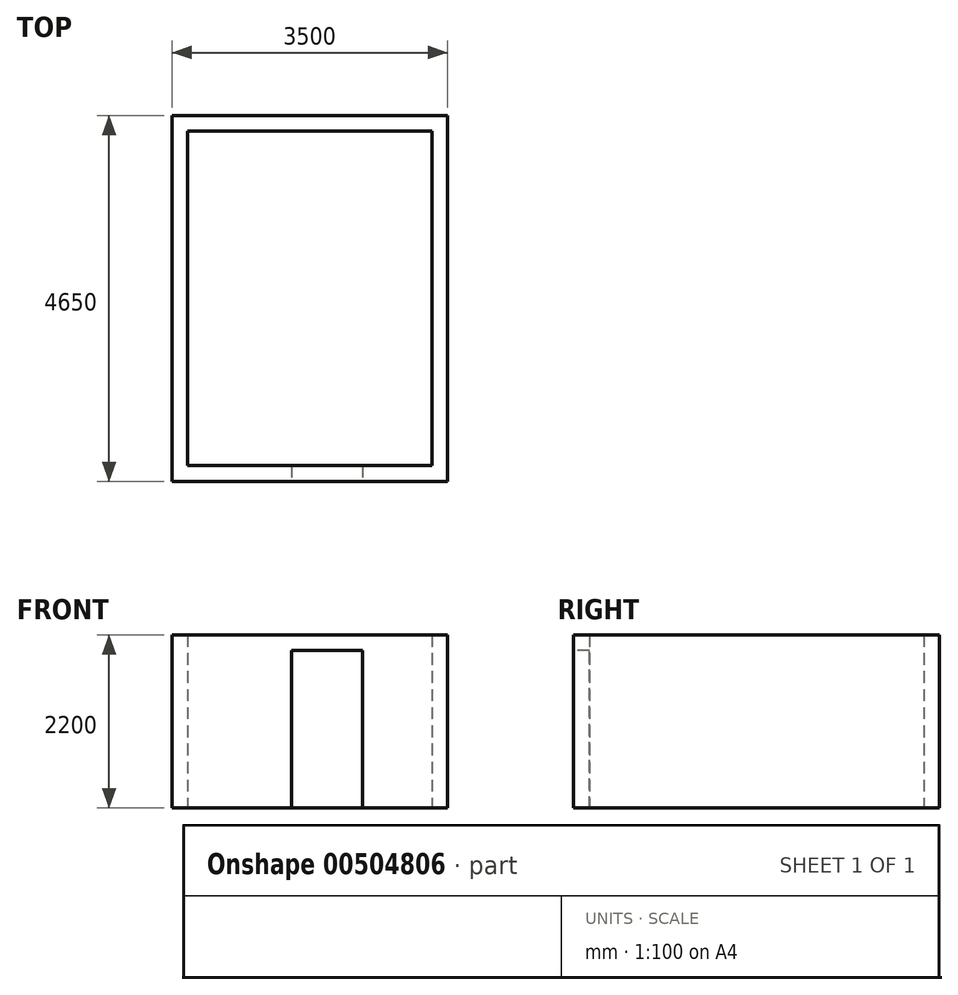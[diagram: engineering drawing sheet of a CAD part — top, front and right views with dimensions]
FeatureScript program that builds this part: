
annotation { "Feature Type Name" : "Feature", "Feature Type Description" : "" }
export const myFeature = defineFeature(function(context is Context, id is Id, definition is map)
    precondition{}
    {
        {
            var Q0;
            Q0=qCreatedBy(makeId("Top.planeOp"),FACE);
            var sketch = newSketch(context, id + "F0", { "sketchPlane" : qUnion([Q0])});
            skLineSegment(sketch, "E0.bottom", {"start": v(500, 4755.13) * mm, "end": v(-3000, 4755.13) * mm});
            skLineSegment(sketch, "E0.top", {"start": v(500, 105.13) * mm, "end": v(-3000, 105.13) * mm});
            skLineSegment(sketch, "E0.right", {"start": v(-3000, 4755.13) * mm, "end": v(-3000, 105.13) * mm});
            skLineSegment(sketch, "E1", {"start": v(500, 4755.13) * mm, "end": v(500, 105.13) * mm});
            skLineSegment(sketch, "E2.0", {"start": v(-2800, 4555.13) * mm, "end": v(-2800, 305.13) * mm});
            skLineSegment(sketch, "E2.1", {"start": v(300, 4555.13) * mm, "end": v(-2800, 4555.13) * mm});
            skLineSegment(sketch, "E2.2", {"start": v(300, 4555.13) * mm, "end": v(300, 305.13) * mm});
            skLineSegment(sketch, "E2.3", {"start": v(300, 305.13) * mm, "end": v(-2800, 305.13) * mm});
            skSolve(sketch);
        }
        {
            var Q0;
            Q0=makeQuery(id+"F0.imprint","IMPRINT",FACE,{"disambiguationData":[TD([[makeQuery(id+"F0.imprint","IMPRINT",EDGE,{"derivedFrom":sQuery(id+"F0.wireOp",EDGE,"E0.bottom")}),1.0]])]});
            extrude(context, id + "F1", {"entities" : qUnion([Q0]), "depth" : 2200 * mm, "offsetDistance" : 25 * mm});
        }
        {
            var Q0;
            Q0=makeQuery(id+"F1.opExtrude","SWEPT_FACE",FACE,{"disambiguationData":[OSD([sQuery(id+"F0.wireOp",EDGE,"E0.top")])]});
            var sketch = newSketch(context, id + "F2", { "sketchPlane" : qUnion([Q0])});
            skLineSegment(sketch, "E3.bottom", {"start": v(-582.1, 0) * mm, "end": v(-1482.1, 0) * mm});
            skLineSegment(sketch, "E3.top", {"start": v(-582.1, 2000) * mm, "end": v(-1482.1, 2000) * mm});
            skLineSegment(sketch, "E3.left", {"start": v(-582.1, 0) * mm, "end": v(-582.1, 2000) * mm});
            skLineSegment(sketch, "E3.right", {"start": v(-1482.1, 0) * mm, "end": v(-1482.1, 2000) * mm});
            skSolve(sketch);
        }
        {
            var Q0;
            Q0 = qSketchRegion(id + "F2", true);
            extrude(context, id + "F3", {"entities" : qUnion([Q0]), "operationType" : NewBodyOperationType.REMOVE, "oppositeDirection" : true, "depth" : 300 * mm, "offsetDistance" : 25 * mm});
        }
    });
